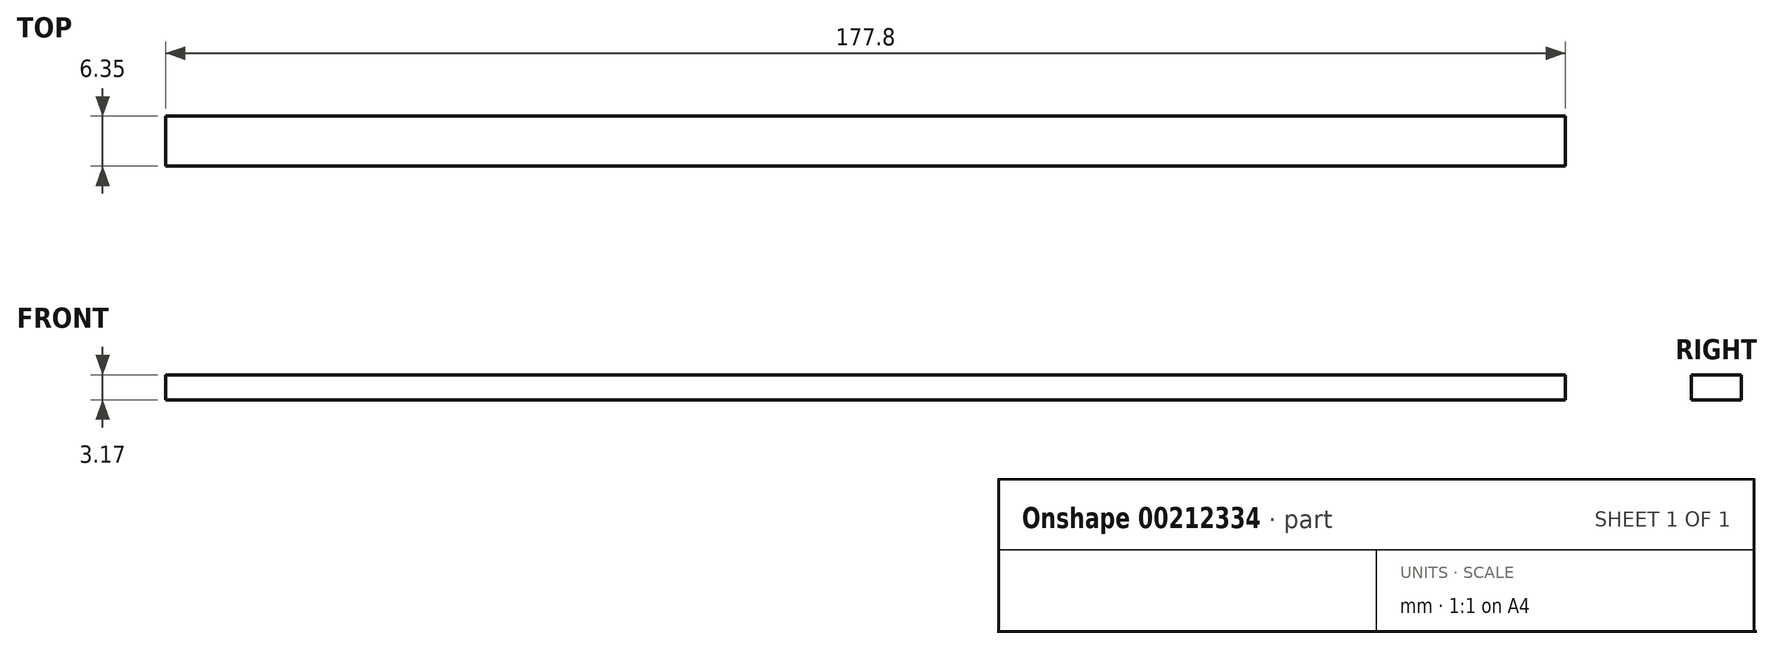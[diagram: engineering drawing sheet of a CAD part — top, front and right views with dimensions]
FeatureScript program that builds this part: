
annotation { "Feature Type Name" : "Feature", "Feature Type Description" : "" }
export const myFeature = defineFeature(function(context is Context, id is Id, definition is map)
    precondition{}
    {
        {
            var Q0;
            Q0=qCreatedBy(makeId("Top.planeOp"),FACE);
            var sketch = newSketch(context, id + "F0", { "sketchPlane" : qUnion([Q0])});
            skLineSegment(sketch, "E0.bottom", {"start": v(0, 0) * mm, "end": v(177.8, 0) * mm});
            skLineSegment(sketch, "E0.top", {"start": v(0, 6.35) * mm, "end": v(177.8, 6.35) * mm});
            skLineSegment(sketch, "E0.left", {"start": v(0, 0) * mm, "end": v(0, 6.35) * mm});
            skLineSegment(sketch, "E0.right", {"start": v(177.8, 0) * mm, "end": v(177.8, 6.35) * mm});
            skSolve(sketch);
        }
        {
            var Q0;
            Q0 = qSketchRegion(id + "F0", true);
            extrude(context, id + "F1", {"entities" : qUnion([Q0]), "depth" : 3.17 * mm});
        }
    });
